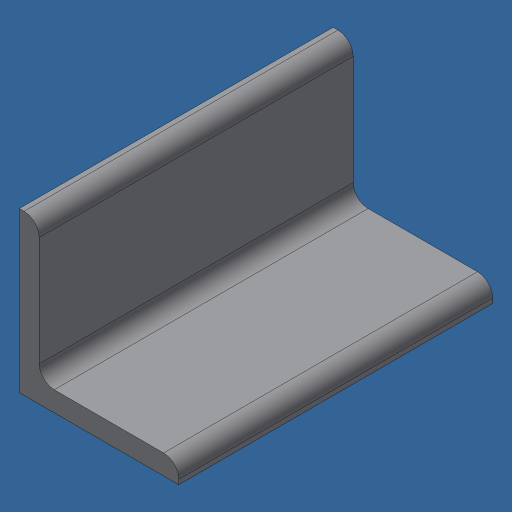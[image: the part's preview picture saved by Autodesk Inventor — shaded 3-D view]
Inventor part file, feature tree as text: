
AUTODESK INVENTOR PART (.ipt)
format: ipt  version: 2024.3 (Build 283343000, 343)  size: 113,664 bytes
history: native  units: mm (DEFAULTED — no unit token found)
features: other x1, extrude x1
ambient origin geometry x8: Origin, YZ Plane, XZ Plane, XY Plane, X Axis, Y Axis, Z Axis, Center Point
bodies: Body1 (feature_tree)
feature tree (2):
  other  "Finish - None"
  extrude  "2" X 2" X 1/4""  Depth=6.35mm
